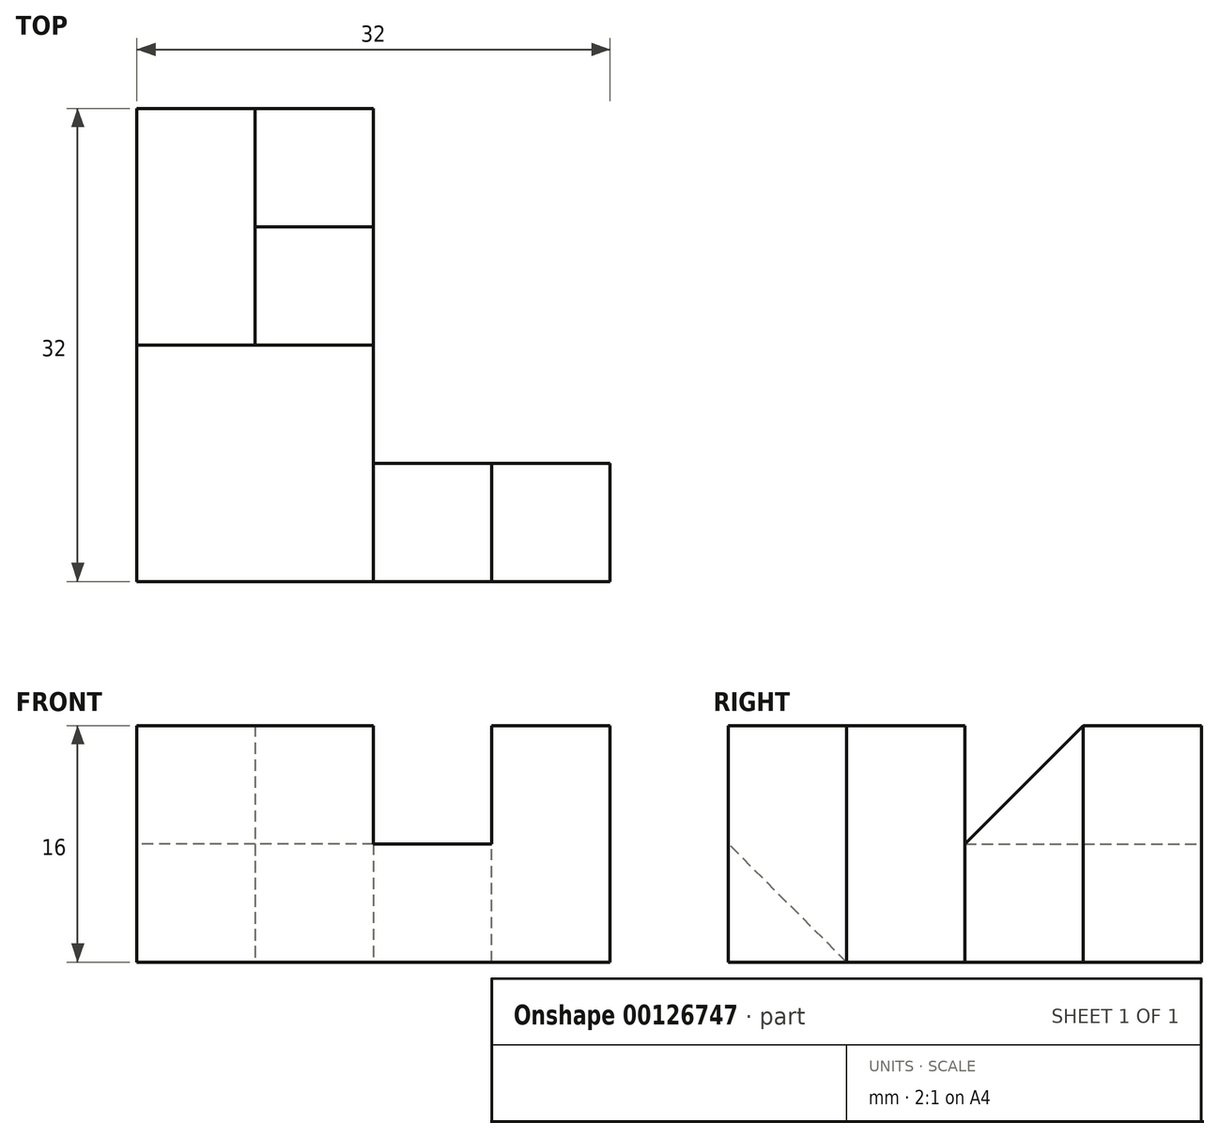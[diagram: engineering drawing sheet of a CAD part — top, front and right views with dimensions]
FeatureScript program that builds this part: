
annotation { "Feature Type Name" : "Feature", "Feature Type Description" : "" }
export const myFeature = defineFeature(function(context is Context, id is Id, definition is map)
    precondition{}
    {
        {
            var Q0;
            Q0=qCreatedBy(makeId("Top.planeOp"),FACE);
            var sketch = newSketch(context, id + "F0", { "sketchPlane" : qUnion([Q0])});
            skLineSegment(sketch, "E0", {"start": v(-30.94, 16) * mm, "end": v(-30.94, -16) * mm});
            skLineSegment(sketch, "E1", {"start": v(-30.94, -16) * mm, "end": v(1.06, -16) * mm});
            skLineSegment(sketch, "E2", {"start": v(1.06, -16) * mm, "end": v(1.06, -8) * mm});
            skLineSegment(sketch, "E3", {"start": v(1.06, -8) * mm, "end": v(-14.94, -8) * mm});
            skLineSegment(sketch, "E4", {"start": v(-14.94, -8) * mm, "end": v(-14.94, 16) * mm});
            skLineSegment(sketch, "E5", {"start": v(-14.94, 16) * mm, "end": v(-30.94, 16) * mm});
            skLineSegment(sketch, "E6", {"start": v(-6.94, -8) * mm, "end": v(-6.94, -16) * mm});
            skLineSegment(sketch, "E7", {"start": v(-14.94, -8) * mm, "end": v(-14.94, -16) * mm});
            skLineSegment(sketch, "E8", {"start": v(-14.94, 0) * mm, "end": v(-30.94, 0) * mm});
            skLineSegment(sketch, "E9", {"start": v(-22.94, 0) * mm, "end": v(-22.94, 16) * mm});
            skLineSegment(sketch, "E10", {"start": v(-22.94, 8) * mm, "end": v(-14.94, 8) * mm});
            skSolve(sketch);
        }
        {
            var Q0;
            {var subQ0=sQuery(id+"F0.wireOp",EDGE,"E2");Q0=makeQuery(id+"F0.imprint","IMPRINT",FACE,{"disambiguationData":[TD([[makeQuery(id+"F0.imprint","IMPRINT",EDGE,{"derivedFrom":subQ0}),1.0]])]});}
            extrude(context, id + "F1", {"entities" : qUnion([Q0]), "depth" : 16 * mm});
        }
        {
            var Q0;
            {var subQ0=sQuery(id+"F0.wireOp",EDGE,"E6");Q0=makeQuery(id+"F0.imprint","IMPRINT",FACE,{"disambiguationData":[TD([[makeQuery(id+"F0.imprint","IMPRINT",EDGE,{"derivedFrom":subQ0}),-1.0]])]});}
            extrude(context, id + "F2", {"entities" : qUnion([Q0]), "operationType" : NewBodyOperationType.ADD, "depth" : 8 * mm});
        }
        {
            var Q0;
            {var subQ0=sQuery(id+"F0.wireOp",EDGE,"E7");Q0=makeQuery(id+"F0.imprint","IMPRINT",FACE,{"disambiguationData":[TD([[makeQuery(id+"F0.imprint","IMPRINT",EDGE,{"derivedFrom":subQ0}),-1.0]])]});}
            extrude(context, id + "F3", {"entities" : qUnion([Q0]), "operationType" : NewBodyOperationType.ADD, "depth" : 16 * mm});
        }
        {
            var Q0;
            {var subQ0=sQuery(id+"F0.wireOp",EDGE,"E5");var subQ1=sQuery(id+"F0.wireOp",EDGE,"E0");var subQ2=makeQuery(id+"F0.imprint","INTERSECT",VERTEX,{"derivedFrom":[subQ1,subQ0]});Q0=makeQuery(id+"F0.imprint","IMPRINT",FACE,{"disambiguationData":[TD([[makeQuery(id+"F0.imprint","IMPRINT",EDGE,{"disambiguationData":[TD([[subQ2,-1.0]])],"derivedFrom":subQ1}),1.0]])]});}
            extrude(context, id + "F4", {"entities" : qUnion([Q0]), "operationType" : NewBodyOperationType.ADD, "depth" : 8 * mm});
        }
        {
            var Q0;
            {var subQ3=sQuery(id+"F0.wireOp",EDGE,"E10");Q0=makeQuery(id+"F0.imprint","IMPRINT",FACE,{"disambiguationData":[TD([[makeQuery(id+"F0.imprint","IMPRINT",EDGE,{"derivedFrom":subQ3}),1.0]])]});}
            extrude(context, id + "F5", {"entities" : qUnion([Q0]), "operationType" : NewBodyOperationType.ADD, "depth" : 16 * mm});
        }
        {
            var Q0;
            {var subQ3=sQuery(id+"F0.wireOp",EDGE,"E10");Q0=makeQuery(id+"F0.imprint","IMPRINT",FACE,{"disambiguationData":[TD([[makeQuery(id+"F0.imprint","IMPRINT",EDGE,{"derivedFrom":subQ3}),-1.0]])]});}
            extrude(context, id + "F6", {"entities" : qUnion([Q0]), "depth" : 16 * mm});
        }
        {
            var Q0;
            Q0=makeQuery(id+"F2.opExtrude","CAP_EDGE",EDGE,{"disambiguationData":[OSD([sQuery(id+"F0.wireOp",EDGE,"E3")])],"isStart":false});
            chamfer(context, id + "F7", {"entities" : qUnion([Q0]), "width" : 8 * mm, "tangentPropagation" : true});
        }
        {
            var Q0;
            Q0=makeQuery(id+"F6.opExtrude","CAP_EDGE",EDGE,{"disambiguationData":[OSD([sQuery(id+"F0.wireOp",EDGE,"E8")])],"isStart":false});
            chamfer(context, id + "F8", {"entities" : qUnion([Q0]), "width" : 8 * mm, "tangentPropagation" : true});
        }
    });
